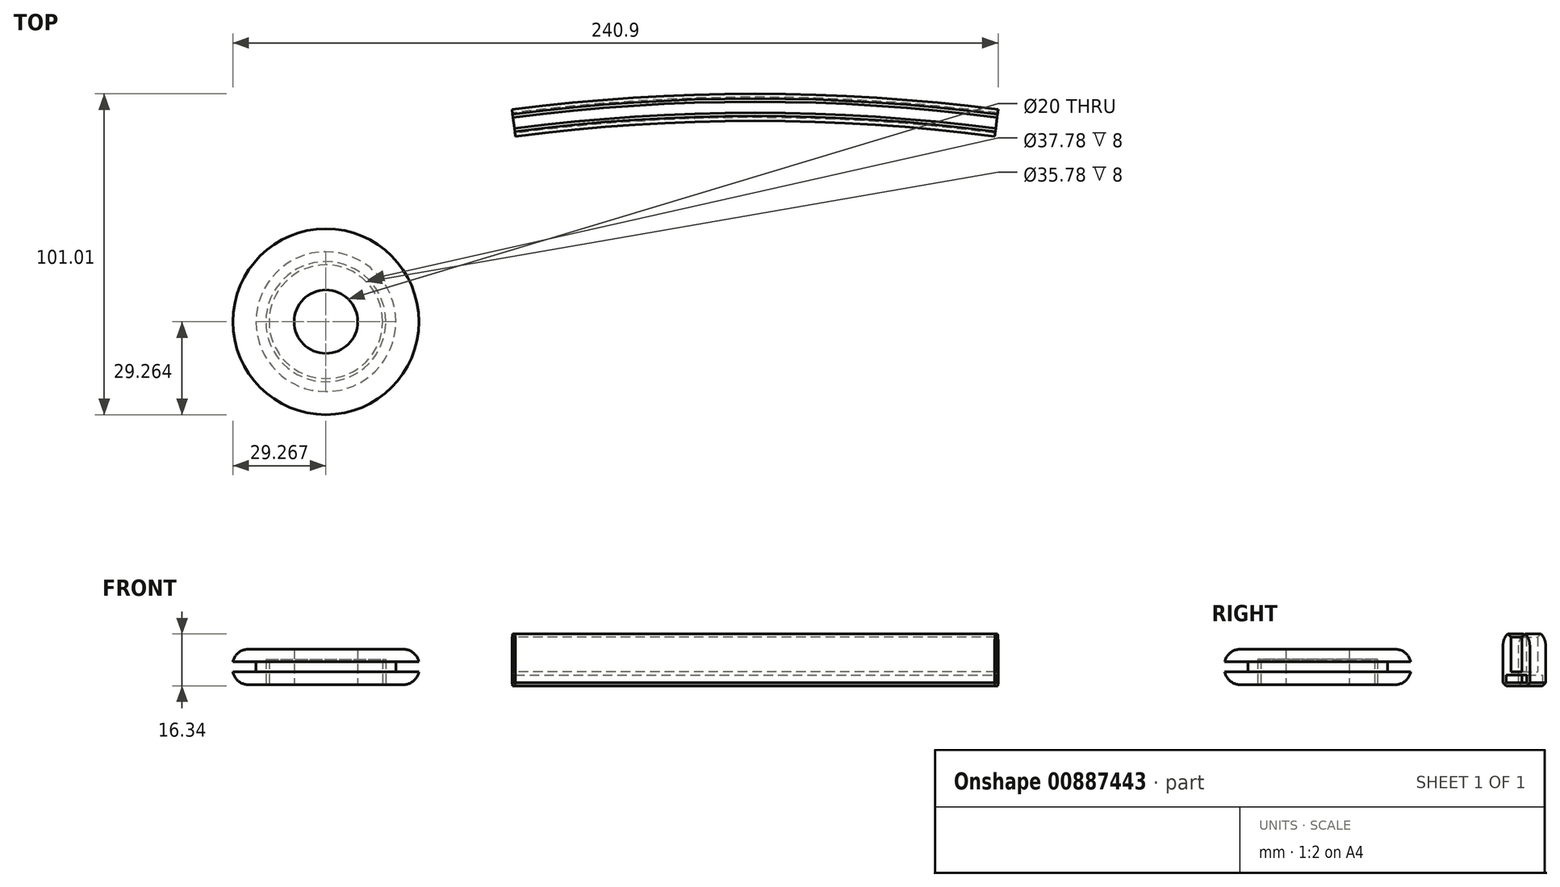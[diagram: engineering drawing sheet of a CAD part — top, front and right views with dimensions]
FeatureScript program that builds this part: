
annotation { "Feature Type Name" : "Feature", "Feature Type Description" : "" }
export const myFeature = defineFeature(function(context is Context, id is Id, definition is map)
    precondition{}
    {
        {
            var Q0;
            Q0=qCreatedBy(makeId("Top.planeOp"),FACE);
            var sketch = newSketch(context, id + "F0", { "sketchPlane" : qUnion([Q0])});
            skLineSegment(sketch, "E0.bottom", {"start": v(76.2, 1.75) * mm, "end": v(-76.2, 1.75) * mm, "construction": true});
            skLineSegment(sketch, "E0.top", {"start": v(76.2, -1.75) * mm, "end": v(-76.2, -1.75) * mm, "construction": true});
            skLineSegment(sketch, "E0.left", {"start": v(76.2, 1.75) * mm, "end": v(76.2, -1.75) * mm});
            skLineSegment(sketch, "E0.right", {"start": v(-76.2, 1.75) * mm, "end": v(-76.2, -1.75) * mm});
            skPoint(sketch, "E0.middle", {"position": v(0, 0) * mm});
            skLineSegment(sketch, "E1.bottom", {"start": v(-76.2, 6.1) * mm, "end": v(76.2, 6.1) * mm});
            skLineSegment(sketch, "E1.top", {"start": v(-76.2, -6.1) * mm, "end": v(76.2, -6.1) * mm});
            skLineSegment(sketch, "E1.left", {"start": v(-76.2, 6.1) * mm, "end": v(-76.2, -6.1) * mm});
            skLineSegment(sketch, "E1.right", {"start": v(76.2, 6.1) * mm, "end": v(76.2, -6.1) * mm});
            skSolve(sketch);
        }
        {
            var Q0;
            Q0 = qSketchRegion(id + "F0", true);
            extrude(context, id + "F1", {"entities" : qUnion([Q0]), "oppositeDirection" : true, "depth" : 1 * mm, "offsetDistance" : 25 * mm});
        }
        {
            var Q0;
            Q0=makeQuery(id+"F1.opExtrude","SWEPT_BODY",BODY,{"disambiguationData":[OSD([sQuery(id+"F0.wireOp",EDGE,"E1.bottom"),sQuery(id+"F0.wireOp",EDGE,"E1.top"),sQuery(id+"F0.wireOp",EDGE,"E1.left"),sQuery(id+"F0.wireOp",EDGE,"E1.right")])]});
            deleteBodies(context, id + "F2", {"entities" : qUnion([Q0])});
        }
        {
            var Q0;
            Q0=qCreatedBy(makeId("Top.planeOp"),FACE);
            var sketch = newSketch(context, id + "F3", { "sketchPlane" : qUnion([Q0])});
            skLineSegment(sketch, "E2.bottom", {"start": v(77.05, 1.75) * mm, "end": v(-75.35, 1.75) * mm, "construction": true});
            skLineSegment(sketch, "E2.top", {"start": v(77.05, -1.75) * mm, "end": v(-75.35, -1.75) * mm, "construction": true});
            skLineSegment(sketch, "E2.left", {"start": v(77.05, 1.75) * mm, "end": v(77.05, -1.75) * mm, "construction": true});
            skLineSegment(sketch, "E2.right", {"start": v(-75.35, 1.75) * mm, "end": v(-75.35, -1.75) * mm, "construction": true});
            skPoint(sketch, "E2.middle", {"position": v(0.85, 0) * mm});
            skArc(sketch, "E3", {"start": v(77.05, 1.75) * mm, "mid": v(0.85, 6.7) * mm, "end": v(-75.35, 1.75) * mm});
            skArc(sketch, "E4.0", {"start": v(77.37, 4.23) * mm, "mid": v(0.85, 9.2) * mm, "end": v(-75.68, 4.23) * mm});
            skArc(sketch, "E5.0", {"start": v(76.6, -1.72) * mm, "mid": v(0.85, 3.2) * mm, "end": v(-74.9, -1.72) * mm});
            skArc(sketch, "E6.0", {"start": v(76.27, -4.2) * mm, "mid": v(0.85, 0.7) * mm, "end": v(-74.58, -4.2) * mm});
            skLineSegment(sketch, "E7", {"start": v(-75.68, 4.23) * mm, "end": v(-74.58, -4.2) * mm});
            skLineSegment(sketch, "E8", {"start": v(77.37, 4.23) * mm, "end": v(76.27, -4.2) * mm});
            skSolve(sketch);
        }
        {
            var Q0;
            {var subQ0=sQuery(id+"F3.wireOp",EDGE,"E5.0");Q0=makeQuery(id+"F3.imprint","IMPRINT",FACE,{"disambiguationData":[TD([[makeQuery(id+"F3.imprint","IMPRINT",EDGE,{"derivedFrom":subQ0}),1.0]])]});}
            var Q1;
            {var subQ0=sQuery(id+"F3.wireOp",EDGE,"E3");Q1=makeQuery(id+"F3.imprint","IMPRINT",FACE,{"disambiguationData":[TD([[makeQuery(id+"F3.imprint","IMPRINT",EDGE,{"derivedFrom":subQ0}),1.0]])]});}
            var Q2;
            {var subQ0=sQuery(id+"F3.wireOp",EDGE,"E3");Q2=makeQuery(id+"F3.imprint","IMPRINT",FACE,{"disambiguationData":[TD([[makeQuery(id+"F3.imprint","IMPRINT",EDGE,{"derivedFrom":subQ0}),-1.0]])]});}
            extrude(context, id + "F4", {"entities" : qUnion([Q0, Q1, Q2]), "oppositeDirection" : true, "depth" : 1 * mm, "offsetDistance" : 25 * mm});
        }
        {
            var Q0;
            Q0=makeQuery(id+"F4.opExtrude","CAP_FACE",FACE,{"disambiguationData":[OSD([sQuery(id+"F3.wireOp",EDGE,"E4.0"),sQuery(id+"F3.wireOp",EDGE,"E6.0"),sQuery(id+"F3.wireOp",EDGE,"E7"),sQuery(id+"F3.wireOp",EDGE,"E8")])],"isStart":true});
            var sketch = newSketch(context, id + "F5", { "sketchPlane" : qUnion([Q0])});
            skArc(sketch, "E9.0", {"start": v(77.05, 1.75) * mm, "mid": v(0.85, 6.7) * mm, "end": v(-75.35, 1.75) * mm});
            skArc(sketch, "E10.0", {"start": v(76.6, -1.72) * mm, "mid": v(0.85, 3.2) * mm, "end": v(-74.9, -1.72) * mm});
            skSolve(sketch);
        }
        {
            var Q0;
            {var subQ0=sQuery(id+"F5.wireOp",EDGE,"E9.0");Q0=makeQuery(id+"F5.imprint","IMPRINT",FACE,{"disambiguationData":[TD([[makeQuery(id+"F5.imprint","IMPRINT",EDGE,{"derivedFrom":subQ0}),-1.0]])]});}
            var Q1;
            {var subQ0=sQuery(id+"F5.wireOp",EDGE,"E10.0");Q1=makeQuery(id+"F5.imprint","IMPRINT",FACE,{"disambiguationData":[TD([[makeQuery(id+"F5.imprint","IMPRINT",EDGE,{"derivedFrom":subQ0}),1.0]])]});}
            extrude(context, id + "F6", {"entities" : qUnion([Q0, Q1]), "operationType" : NewBodyOperationType.ADD, "depth" : 12 * mm, "offsetDistance" : 25 * mm});
        }
        {
            var Q0;
            Q0=makeQuery(id+"F6.opExtrude","CAP_EDGE",EDGE,{"disambiguationData":[OSD([sQuery(id+"F5.wireOp",EDGE,"E9.0")])],"isStart":false});
            var Q1;
            Q1=makeQuery(id+"F6.opExtrude","CAP_EDGE",EDGE,{"disambiguationData":[OSD([sQuery(id+"F5.wireOp",EDGE,"E10.0")])],"isStart":false});
            chamfer(context, id + "F7", {"entities" : qUnion([Q0, Q1]), "width" : 1 * mm, "tangentPropagation" : true});
        }
        {
            var Q0;
            Q0=makeQuery(id+"F6.opExtrude","CAP_EDGE",EDGE,{"disambiguationData":[OSD([sQuery(id+"F3.wireOp",EDGE,"E6.0")])],"isStart":false});
            var Q1;
            Q1=makeQuery(id+"F6.opExtrude","CAP_EDGE",EDGE,{"disambiguationData":[OSD([sQuery(id+"F3.wireOp",EDGE,"E4.0")])],"isStart":false});
            fillet(context, id + "F8", {"entities" : qUnion([Q0, Q1]), "radius" : 5 * mm, "tangentPropagation" : true, "allowEdgeOverflow" : false});
        }
        {
            var Q0;
            {var subQ0=sQuery(id+"F3.wireOp",EDGE,"E7");var subQ1=makeQuery(id+"F4.opExtrude","CAP_EDGE",EDGE,{"disambiguationData":[OSD([subQ0])],"isStart":true});Q0=makeQuery(id+"F6.boolean.opBoolean","MERGE",FACE,{"derivedFrom":[makeQuery(id+"F4.opExtrude","SWEPT_FACE",FACE,{"disambiguationData":[OSD([subQ0])]}),makeQuery(id+"F6.opExtrude","SWEPT_FACE",FACE,{"disambiguationData":[OSD([subQ0]),TDD([makeQuery(id+"F5.imprint","IMPRINT",EDGE,{"disambiguationData":[TD([[makeQuery(id+"F5.imprint","INTERSECT",VERTEX,{"derivedFrom":[makeQuery(id+"F4.opExtrude","CAP_EDGE",EDGE,{"disambiguationData":[OSD([sQuery(id+"F3.wireOp",EDGE,"E4.0")])],"isStart":true}),subQ1]}),-1.0]])],"derivedFrom":subQ1})])]}),makeQuery(id+"F6.opExtrude","SWEPT_FACE",FACE,{"disambiguationData":[OSD([subQ0]),TDD([makeQuery(id+"F5.imprint","IMPRINT",EDGE,{"disambiguationData":[TD([[makeQuery(id+"F5.imprint","INTERSECT",VERTEX,{"derivedFrom":[makeQuery(id+"F4.opExtrude","CAP_EDGE",EDGE,{"disambiguationData":[OSD([sQuery(id+"F3.wireOp",EDGE,"E6.0")])],"isStart":true}),subQ1]}),1.0]])],"derivedFrom":subQ1})])]})]});}
            var sketch = newSketch(context, id + "F9", { "sketchPlane" : qUnion([Q0])});
            skLineSegment(sketch, "E11.bottom", {"start": v(-5.5, -1) * mm, "end": v(-14, -1) * mm});
            skLineSegment(sketch, "E11.top", {"start": v(-5.5, -4.34) * mm, "end": v(-14, -4.34) * mm});
            skLineSegment(sketch, "E11.left", {"start": v(-5.5, -1) * mm, "end": v(-5.5, -4.34) * mm});
            skLineSegment(sketch, "E11.right", {"start": v(-14, -1) * mm, "end": v(-14, -4.34) * mm});
            skLineSegment(sketch, "E12.0", {"start": v(-6.5, -3.34) * mm, "end": v(-13, -3.34) * mm});
            skLineSegment(sketch, "E13.0", {"start": v(-6.5, -1) * mm, "end": v(-6.5, -3.34) * mm});
            skLineSegment(sketch, "E14.0", {"start": v(-13, -1) * mm, "end": v(-13, -3.34) * mm});
            skSolve(sketch);
        }
        {
            var Q0;
            Q0=makeQuery(id+"F9.imprint","IMPRINT",FACE,{"disambiguationData":[TD([[makeQuery(id+"F9.imprint","IMPRINT",EDGE,{"derivedFrom":sQuery(id+"F9.wireOp",EDGE,"E11.top")}),-1.0]])]});
            var Q1;
            Q1=makeQuery(id+"F4.opExtrude","CAP_EDGE",EDGE,{"disambiguationData":[OSD([sQuery(id+"F3.wireOp",EDGE,"E6.0")])],"isStart":false});
            sweep(context, id + "F10", {"operationType" : NewBodyOperationType.ADD, "profiles" : qUnion([Q0]), "path" : qUnion([Q1])});
        }
        {
            var Q0;
            Q0=makeQuery(id+"F10.opSweep","SWEPT_EDGE",EDGE,{"disambiguationData":[OSD([sQuery(id+"F3.wireOp",EDGE,"E6.0"),sQuery(id+"F9.wireOp",EDGE,"E11.top"),sQuery(id+"F9.wireOp",EDGE,"E11.left")])]});
            var Q1;
            Q1=makeQuery(id+"F10.opSweep","SWEPT_EDGE",EDGE,{"disambiguationData":[OSD([sQuery(id+"F3.wireOp",EDGE,"E6.0"),sQuery(id+"F9.wireOp",EDGE,"E11.top"),sQuery(id+"F9.wireOp",EDGE,"E11.right")])]});
            chamfer(context, id + "F11", {"entities" : qUnion([Q0, Q1]), "width" : 1 * mm, "tangentPropagation" : true});
        }
        {
            var Q0;
            Q0=qCreatedBy(makeId("Top.planeOp"),FACE);
            var sketch = newSketch(context, id + "F12", { "sketchPlane" : qUnion([Q0])});
            skCircle(sketch, "E15", {"center": v(-134.26, -62.54) * mm, "radius": 22 * mm});
            skCircle(sketch, "E16", {"center": v(-134.26, -62.54) * mm, "radius": 10 * mm});
            skSolve(sketch);
        }
        {
            var Q0;
            Q0 = qSketchRegion(id + "F12", true);
            extrude(context, id + "F13", {"entities" : qUnion([Q0]), "depth" : 3.17 * mm, "offsetDistance" : 25 * mm});
        }
        {
            var Q0;
            Q0=makeQuery(id+"F13.opExtrude","CAP_FACE",FACE,{"disambiguationData":[OSD([sQuery(id+"F12.wireOp",EDGE,"E15"),sQuery(id+"F12.wireOp",EDGE,"E16")])],"isStart":false});
            var sketch = newSketch(context, id + "F14", { "sketchPlane" : qUnion([Q0])});
            skCircle(sketch, "E17", {"center": v(-134.26, -62.54) * mm, "radius": 29.27 * mm});
            skSolve(sketch);
        }
        {
            var Q0;
            Q0 = qSketchRegion(id + "F14", true);
            extrude(context, id + "F15", {"entities" : qUnion([Q0]), "operationType" : NewBodyOperationType.ADD, "depth" : 4 * mm, "offsetDistance" : 25 * mm});
        }
        {
            var Q0;
            Q0=makeQuery(id+"F15.opExtrude","CAP_EDGE",EDGE,{"disambiguationData":[OSD([sQuery(id+"F14.wireOp",EDGE,"E17")])],"isStart":false});
            fillet(context, id + "F16", {"entities" : qUnion([Q0]), "radius" : 5 * mm, "tangentPropagation" : true, "allowEdgeOverflow" : false});
        }
        {
            var Q0;
            Q0=makeQuery(id+"F15.boolean.opBoolean","SPLIT",FACE,{"disambiguationData":[TD([makeQuery(id+"F13.opExtrude","SWEPT_FACE",FACE,{"disambiguationData":[OSD([sQuery(id+"F12.wireOp",EDGE,"E16")])]})])],"derivedFrom":makeQuery(id+"F15.opExtrude","CAP_FACE",FACE,{"disambiguationData":[OSD([sQuery(id+"F14.wireOp",EDGE,"E17")])],"isStart":true})});
            extrude(context, id + "F17", {"entities" : qUnion([Q0]), "operationType" : NewBodyOperationType.REMOVE, "oppositeDirection" : true, "depth" : 25 * mm, "offsetDistance" : 25 * mm});
        }
        {
            var Q0;
            Q0=makeQuery(id+"F13.opExtrude","CAP_FACE",FACE,{"disambiguationData":[OSD([sQuery(id+"F12.wireOp",EDGE,"E15"),sQuery(id+"F12.wireOp",EDGE,"E16")])],"isStart":true});
            var sketch = newSketch(context, id + "F18", { "sketchPlane" : qUnion([Q0])});
            skCircle(sketch, "E18.0", {"center": v(-134.26, 62.54) * mm, "radius": 29.27 * mm});
            skCircle(sketch, "E19.0", {"center": v(-134.26, 62.54) * mm, "radius": 10 * mm});
            skSolve(sketch);
        }
        {
            var Q0;
            Q0 = qSketchRegion(id + "F18", true);
            extrude(context, id + "F19", {"entities" : qUnion([Q0]), "operationType" : NewBodyOperationType.ADD, "depth" : 4 * mm, "offsetDistance" : 25 * mm});
        }
        {
            var Q0;
            Q0=makeQuery(id+"F19.opExtrude","CAP_EDGE",EDGE,{"disambiguationData":[OSD([sQuery(id+"F18.wireOp",EDGE,"E18.0")])],"isStart":false});
            fillet(context, id + "F20", {"entities" : qUnion([Q0]), "radius" : 5 * mm, "tangentPropagation" : true, "allowEdgeOverflow" : false});
        }
        {
            var Q0;
            Q0=makeQuery(id+"F19.opExtrude","CAP_FACE",FACE,{"disambiguationData":[OSD([sQuery(id+"F18.wireOp",EDGE,"E18.0"),sQuery(id+"F18.wireOp",EDGE,"E19.0")])],"isStart":false});
            var sketch = newSketch(context, id + "F21", { "sketchPlane" : qUnion([Q0])});
            skCircle(sketch, "E20", {"center": v(-134.26, 62.54) * mm, "radius": 18.89 * mm});
            skCircle(sketch, "E21.0", {"center": v(-134.26, 62.54) * mm, "radius": 17.89 * mm});
            skSolve(sketch);
        }
        {
            var Q0;
            Q0=makeQuery(id+"F21.imprint","IMPRINT",FACE,{"disambiguationData":[TD([[makeQuery(id+"F21.imprint","IMPRINT",EDGE,{"derivedFrom":sQuery(id+"F21.wireOp",EDGE,"E20")}),1.0]])]});
            extrude(context, id + "F22", {"entities" : qUnion([Q0]), "oppositeDirection" : true, "depth" : 8 * mm, "offsetDistance" : 25 * mm});
        }
        {
            var Q0;
            Q0=makeQuery(id+"F22.opExtrude","SWEPT_BODY",BODY,{"disambiguationData":[OSD([sQuery(id+"F21.wireOp",EDGE,"E20"),sQuery(id+"F21.wireOp",EDGE,"E21.0")])]});
            var Q1;
            Q1=makeQuery(id+"F13.opExtrude","SWEPT_BODY",BODY,{"disambiguationData":[OSD([sQuery(id+"F12.wireOp",EDGE,"E15"),sQuery(id+"F12.wireOp",EDGE,"E16")])]});
            booleanBodies(context, id + "F23", {"operationType" : BooleanOperationType.SUBTRACTION, "tools" : qUnion([Q0]), "targets" : qUnion([Q1]), "keepTools" : true});
        }
    });
